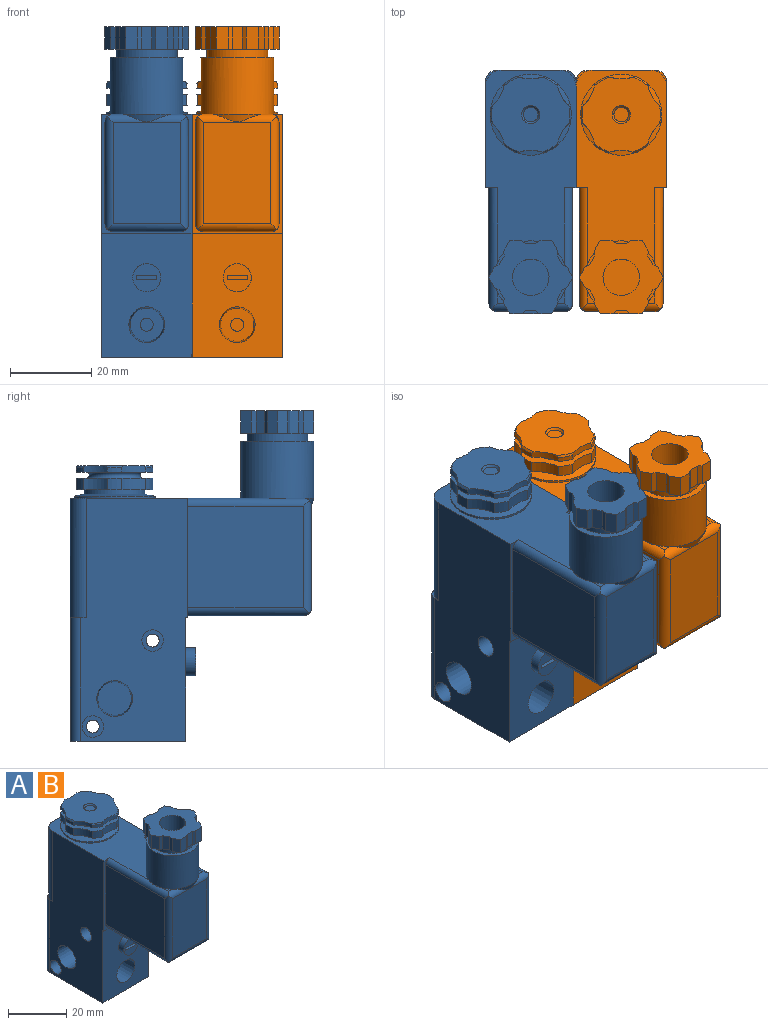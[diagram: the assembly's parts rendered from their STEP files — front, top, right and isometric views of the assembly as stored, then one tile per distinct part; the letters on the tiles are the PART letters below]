
ASSEMBLY  parts=2 mates=1
PART A: 143 faces, bbox 22.3x60.1x81.4 mm
  f0: plane 5.5x2.95mm, normal (0,-1,0), area 16.2mm2, adj f1,f29,f139,f140
  f1: plane 5.5x1mm, normal (0.57,-0.82,0), area 6.7mm2, adj f0,f2,f29,f140
  f2: plane 5.5x2.5mm, normal (0,-1,0), area 13.8mm2, adj f1,f3,f29,f140
  f3: plane 5.5x1mm, normal (-0.57,-0.82,0), area 6.7mm2, adj f2,f4,f29,f140
  f4: plane 5.5x2.95mm, normal (0,-1,0), area 16.2mm2, adj f3,f5,f29,f140
  f5: plane 5.5x2.55mm, normal (0.87,-0.5,0), area 16.2mm2, adj f4,f6,f29,f140
  f6: plane 5.5x1.22mm, normal (1,0.09,0), area 6.7mm2, adj f5,f7,f29,f140
  f7: plane 5.5x2.17mm, normal (0.87,-0.5,0), area 13.8mm2, adj f6,f8,f29,f140
  f8: plane 5.5x1.11mm, normal (0.42,-0.91,0), area 6.7mm2, adj f7,f9,f29,f140
  f9: plane 5.5x2.55mm, normal (0.87,-0.5,0), area 16.2mm2, adj f8,f10,f29,f140
  f10: plane 5.5x2.55mm, normal (0.87,0.5,0), area 16.2mm2, adj f9,f11,f29,f140
  f11: plane 5.5x1.11mm, normal (0.42,0.91,0), area 6.7mm2, adj f10,f12,f29,f140
  f12: plane 5.5x2.17mm, normal (0.87,0.5,0), area 13.8mm2, adj f11,f13,f29,f140
  f13: plane 5.5x1.22mm, normal (1,-0.09,0), area 6.7mm2, adj f12,f14,f29,f140
  f14: plane 5.5x2.55mm, normal (0.87,0.5,0), area 16.2mm2, adj f13,f15,f29,f140
  f15: plane 5.5x2.95mm, normal (0,1,0), area 16.2mm2, adj f14,f16,f29,f140
  f16: plane 5.5x1mm, normal (-0.57,0.82,0), area 6.7mm2, adj f15,f17,f29,f140
  f17: plane 5.5x2.5mm, normal (0,1,0), area 13.8mm2, adj f16,f18,f29,f140
  f18: plane 5.5x1mm, normal (0.57,0.82,0), area 6.7mm2, adj f17,f19,f29,f140
  f19: plane 5.5x2.95mm, normal (0,1,0), area 16.2mm2, adj f18,f20,f29,f140
  f20: plane 5.5x2.55mm, normal (-0.87,0.5,0), area 16.2mm2, adj f19,f21,f29,f140
  f21: plane 5.5x1.22mm, normal (-1,-0.09,0), area 6.7mm2, adj f20,f22,f29,f140
  f22: plane 5.5x2.17mm, normal (-0.87,0.5,0), area 13.8mm2, adj f21,f23,f29,f140
  f23: plane 5.5x1.11mm, normal (-0.42,0.91,0), area 6.7mm2, adj f22,f24,f29,f140
  f24: plane 5.5x2.55mm, normal (-0.87,0.5,0), area 16.2mm2, adj f23,f25,f29,f140
  f25: plane 5.5x2.55mm, normal (-0.87,-0.5,0), area 16.2mm2, adj f24,f26,f29,f140
  f26: plane 5.5x1.11mm, normal (-0.42,-0.91,0), area 6.7mm2, adj f25,f27,f29,f140
  f27: plane 5.5x2.17mm, normal (-0.87,-0.5,0), area 13.8mm2, adj f26,f28,f29,f140
  f28: plane 5.5x1.22mm, normal (-1,0.09,0), area 6.7mm2, adj f27,f29,f139,f140
  f29: plane 20.78x18mm, normal (0,0,-1), area 89.2mm2, adj f0,f1,f2,f3,f4,f5,f6,f7
  f30: cylinder r=7.5mm len=15mm, axis (0,0,-1), area 94.2mm2, adj f29,f31
  f31: plane 18x18mm, normal (0,0,1), area 77.8mm2, adj f30,f32
  f32: cylinder r=9mm len=18mm, axis (0,0,-1), area 791.7mm2, adj f31,f33,f93,f94,f95,f96,f97,f98
  f33: cone r=298.57mm half-angle=17.4deg, axis (0,0,1), area 0mm2, adj f32,f34
  f34: cylinder r=2mm len=29.91mm, axis (0,-1,0), area 88.6mm2, adj f33,f35,f91,f92,f93,f95,f98
  f35: plane 29.5x22.3mm, normal (0,-1,0), area 63.9mm2, adj f34,f36,f40,f41,f42,f43,f86,f87
  f36: plane 28.5x25mm, normal (-1,0,0), area 712.5mm2, adj f35,f37,f40,f90
  f37: cylinder r=2mm len=27.83mm, axis (0,0,1), area 83mm2, adj f36,f38,f39,f40,f90,f95
  f38: plane 25x16.6mm, normal (0,-1,0), area 415mm2, adj f37,f39,f92,f95
  f39: cylinder r=2mm len=19.43mm, axis (1,0,0), area 56.6mm2, adj f37,f38,f40,f41,f42,f92
  f40: cylinder r=2mm len=29.91mm, axis (0,-1,0), area 91.8mm2, adj f35,f36,f37,f39,f41
  f41: plane 28.5x16.6mm, normal (0,0,-1), area 473.1mm2, adj f35,f39,f40,f42
  f42: cylinder r=2mm len=29.91mm, axis (0,-1,0), area 91.8mm2, adj f35,f39,f41,f91,f92
  f43: plane 59.9x26.4mm, normal (1,0,0), area 1419.7mm2, adj f35,f44,f49,f54,f56,f68,f75,f76
  f44: cylinder r=2.65mm len=8mm, axis (-1,0,0), area 133.2mm2, adj f43,f45
  f45: plane 5.3x5.3mm, normal (1,0,0), area 14mm2, adj f44,f46
  f46: cylinder r=1.6mm len=6.3mm, axis (-1,0,0), area 63.3mm2, adj f45,f47
  f47: plane 5.3x5.3mm, normal (-1,0,0), area 14mm2, adj f46,f48
  f48: cylinder r=2.65mm len=8mm, axis (-1,0,0), area 133.2mm2, adj f47,f87
  f49: cylinder r=2.65mm len=8mm, axis (-1,0,0), area 133.2mm2, adj f43,f50
  f50: plane 5.3x5.3mm, normal (1,0,0), area 14mm2, adj f49,f51
  f51: cylinder r=1.6mm len=6.3mm, axis (-1,0,0), area 63.3mm2, adj f50,f52
  f52: plane 5.3x5.3mm, normal (-1,0,0), area 14mm2, adj f51,f53
  f53: cylinder r=2.65mm len=8mm, axis (-1,0,0), area 133.2mm2, adj f52,f87
  f54: cone r=4.15mm half-angle=1.8deg, axis (1,0,0), area 223.2mm2, adj f43,f55
  f55: plane 8.3x8.3mm, normal (1,0,0), area 54.1mm2, adj f54
  f56: plane 30.4x22.3mm, normal (0,-1,0), area 579.5mm2, adj f43,f57,f61,f77,f86,f87
  f57: cone r=4.41mm half-angle=1.8deg, axis (0,-1,0), area 267.3mm2, adj f56,f58
  f58: plane 8.19x8.19mm, normal (0,-1,0), area 44.7mm2, adj f57,f59
  f59: cylinder r=1.6mm len=3.2mm, axis (0,-1,0), area 30.2mm2, adj f58,f60
  f60: plane 3.2x3.2mm, normal (0,-1,0), area 8mm2, adj f59
  f61: cylinder r=3.45mm len=6.9mm, axis (0,-1,0), area 54.2mm2, adj f56,f62
  f62: plane 6.9x6.9mm, normal (0,-1,0), area 32.4mm2, adj f61,f63,f65,f66,f67
  f63: plane 5x1mm, normal (0,0,1), area 5mm2, adj f62,f64,f65,f67
  f64: plane 5x1mm, normal (0,-1,0), area 5mm2, adj f63,f65,f66,f67
  f65: plane 1x1mm, normal (-1,0,0), area 1mm2, adj f62,f63,f64,f66
  f66: plane 5x1mm, normal (0,0,-1), area 5mm2, adj f62,f64,f65,f67
  f67: plane 1x1mm, normal (1,0,0), area 1mm2, adj f62,f63,f64,f66
  f68: cylinder r=4mm len=29.5mm, axis (0,0,1), area 185.4mm2, adj f43,f69,f74,f75,f98
  f69: plane 29.5x14.3mm, normal (0,1,0), area 421.9mm2, adj f68,f70,f74,f98
  f70: cylinder r=4mm len=29.5mm, axis (0,0,1), area 185.4mm2, adj f69,f71,f74,f87,f98
  f71: plane 3.9x3.11mm, normal (0,0,1), area 1.8mm2, adj f70,f72,f73,f87
  f72: cylinder r=2.5mm len=30.4mm, axis (0,0,1), area 119.4mm2, adj f71,f73,f77,f87
  f73: plane 30.4x17.3mm, normal (0,1,0), area 525.9mm2, adj f71,f72,f74,f75,f76,f77
  f74: plane 16.08x0.1mm, normal (0,0,-1), area 1.5mm2, adj f68,f69,f70,f73
  f75: plane 3.9x3.11mm, normal (0,0,1), area 1.8mm2, adj f43,f68,f73,f76
  f76: cylinder r=2.5mm len=30.4mm, axis (0,0,1), area 119.4mm2, adj f43,f73,f75,f77
  f77: plane 28.4x22.3mm, normal (0,0,-1), area 605.5mm2, adj f43,f56,f72,f73,f76,f78,f82,f87
  f78: cone r=2mm half-angle=45deg, axis (0,0,-1), area 6.1mm2, adj f77,f79
  f79: cylinder r=1.62mm len=7.24mm, axis (0,0,-1), area 73.8mm2, adj f78,f80
  f80: cone r=1.62mm half-angle=45deg, axis (0,0,1), area 6.1mm2, adj f79,f81
  f81: plane 4x4mm, normal (0,0,-1), area 12.6mm2, adj f80
  f82: cone r=2mm half-angle=45deg, axis (0,0,-1), area 6.1mm2, adj f77,f83
  f83: cylinder r=1.62mm len=7.24mm, axis (0,0,-1), area 73.8mm2, adj f82,f84
  f84: cone r=1.62mm half-angle=45deg, axis (0,0,1), area 6.1mm2, adj f83,f85
  f85: plane 4x4mm, normal (0,0,-1), area 12.6mm2, adj f84
  f86: plane 22.3x0.5mm, normal (0,0,-1), area 11.1mm2, adj f35,f43,f56,f87
  f87: plane 59.9x26.4mm, normal (-1,0,0), area 1419.7mm2, adj f35,f48,f53,f56,f70,f71,f72,f77
  f88: cone r=4.41mm half-angle=1.8deg, axis (-1,0,0), area 223.2mm2, adj f87,f89
  f89: plane 8.3x8.3mm, normal (-1,0,0), area 54.1mm2, adj f88
  f90: cylinder r=2mm len=29.91mm, axis (0,-1,0), area 88.6mm2, adj f35,f36,f37,f95,f96,f97,f98
  f91: plane 28.5x25mm, normal (1,0,0), area 712.5mm2, adj f34,f35,f42,f92
  f92: cylinder r=2mm len=27.83mm, axis (0,0,1), area 83mm2, adj f34,f38,f39,f42,f91,f95
  f93: plane 2.92x1.97mm, normal (0,0,1), area 2.5mm2, adj f32,f34,f95
  f94: cone r=298.57mm half-angle=17.4deg, axis (0,0,1), area 0mm2, adj f32,f95
  f95: cylinder r=2mm len=19.43mm, axis (1,0,0), area 32.5mm2, adj f32,f34,f37,f38,f90,f92,f93,f94
  f96: plane 2.92x1.97mm, normal (0,0,1), area 2.5mm2, adj f32,f90,f95
  f97: cone r=298.57mm half-angle=17.4deg, axis (0,0,1), area 0mm2, adj f32,f90
  f98: plane 47.62x22.3mm, normal (0,0,1), area 568.6mm2, adj f32,f34,f35,f43,f68,f69,f70,f87
  f99: cylinder r=10mm len=20mm, axis (0,0,1), area 31.4mm2, adj f98,f100
  f100: cone r=7.5mm half-angle=78.7deg, axis (0,0,-1), area 140.2mm2, adj f99,f101
  f101: cylinder r=7.5mm len=15mm, axis (0,0,1), area 47.1mm2, adj f100,f102
  f102: plane 20x18.83mm, normal (0,0,-1), area 104.9mm2, adj f101,f103,f128,f129,f130,f131,f132,f133
  f103: cylinder r=9.5mm len=6.73mm, axis (0,0,-1), area 19.6mm2, adj f102,f104,f128,f138
  f104: plane 20x18.83mm, normal (0,0,1), area 127.7mm2, adj f103,f105,f128,f129,f130,f131,f132,f133
  f105: torus R=7mm, axis (0,0,-1), area 96.6mm2, adj f104,f106
  f106: plane 20x18.83mm, normal (0,0,-1), area 127.7mm2, adj f105,f107,f117,f118,f119,f120,f121,f122
  f107: cylinder r=9.5mm len=6.73mm, axis (0,0,-1), area 11.1mm2, adj f106,f108,f109,f116,f117,f127
  f108: cone r=9.66mm half-angle=33.9deg, axis (0,0,-1), area 2.4mm2, adj f107,f109,f117,f118
  f109: plane 19.33x18.47mm, normal (0,0,1), area 258.1mm2, adj f107,f108,f110,f112,f113,f114,f115,f116
  f110: cone r=1.8mm half-angle=40.4deg, axis (0,0,1), area 8.3mm2, adj f109,f111
  f111: plane 3.6x3.6mm, normal (0,0,1), area 10.2mm2, adj f110
  f112: cone r=9.66mm half-angle=33.9deg, axis (0,0,-1), area 2.4mm2, adj f109,f124,f125,f126
  f113: cone r=9.66mm half-angle=33.9deg, axis (0,0,-1), area 2.4mm2, adj f109,f122,f123,f124
  f114: cone r=9.66mm half-angle=33.9deg, axis (0,0,-1), area 2.4mm2, adj f109,f120,f121,f122
  f115: cone r=9.66mm half-angle=33.9deg, axis (0,0,-1), area 2.4mm2, adj f109,f118,f119,f120
  f116: cone r=9.66mm half-angle=33.9deg, axis (0,0,-1), area 2.4mm2, adj f107,f109,f126,f127
  f117: cylinder r=10mm len=3.11mm, axis (0,0,1), area 4.1mm2, adj f106,f107,f108,f118
  f118: cylinder r=9.5mm len=5.83mm, axis (0,0,-1), area 11.1mm2, adj f106,f108,f109,f115,f117,f119
  f119: cylinder r=10mm len=3.59mm, axis (0,0,1), area 4.1mm2, adj f106,f115,f118,f120
  f120: cylinder r=9.5mm len=5.83mm, axis (0,0,-1), area 11.1mm2, adj f106,f109,f114,f115,f119,f121
  f121: cylinder r=10mm len=3.11mm, axis (0,0,1), area 4.1mm2, adj f106,f114,f120,f122
  f122: cylinder r=9.5mm len=6.73mm, axis (0,0,-1), area 11.1mm2, adj f106,f109,f113,f114,f121,f123
  f123: cylinder r=10mm len=3.11mm, axis (0,0,1), area 4.1mm2, adj f106,f113,f122,f124
  f124: cylinder r=9.5mm len=5.83mm, axis (0,0,-1), area 11.1mm2, adj f106,f109,f112,f113,f123,f125
  f125: cylinder r=10mm len=3.59mm, axis (0,0,1), area 4.1mm2, adj f106,f112,f124,f126
  f126: cylinder r=9.5mm len=5.83mm, axis (0,0,-1), area 11.1mm2, adj f106,f109,f112,f116,f125,f127
  f127: cylinder r=10mm len=3.11mm, axis (0,0,1), area 4.1mm2, adj f106,f107,f116,f126
  f128: cylinder r=10mm len=3.11mm, axis (0,0,1), area 10.3mm2, adj f102,f103,f104,f129
  f129: cylinder r=9.5mm len=5.83mm, axis (0,0,-1), area 19.6mm2, adj f102,f104,f128,f130
  f130: cylinder r=10mm len=3.59mm, axis (0,0,1), area 10.3mm2, adj f102,f104,f129,f131
  f131: cylinder r=9.5mm len=5.83mm, axis (0,0,-1), area 19.6mm2, adj f102,f104,f130,f132
  f132: cylinder r=10mm len=3.11mm, axis (0,0,1), area 10.3mm2, adj f102,f104,f131,f133
  f133: cylinder r=9.5mm len=6.73mm, axis (0,0,-1), area 19.6mm2, adj f102,f104,f132,f134
  f134: cylinder r=10mm len=3.11mm, axis (0,0,1), area 10.3mm2, adj f102,f104,f133,f135
  f135: cylinder r=9.5mm len=5.83mm, axis (0,0,-1), area 19.6mm2, adj f102,f104,f134,f136
  f136: cylinder r=10mm len=3.59mm, axis (0,0,1), area 10.3mm2, adj f102,f104,f135,f137
  f137: cylinder r=9.5mm len=5.83mm, axis (0,0,-1), area 19.6mm2, adj f102,f104,f136,f138
  f138: cylinder r=10mm len=3.11mm, axis (0,0,1), area 10.3mm2, adj f102,f103,f104,f137
  f139: plane 5.5x2.55mm, normal (-0.87,-0.5,0), area 16.2mm2, adj f0,f28,f29,f140
  f140: plane 20.78x18mm, normal (0,0,1), area 202.3mm2, adj f0,f1,f2,f3,f4,f5,f6,f7
  f141: cylinder r=4.5mm len=21.5mm, axis (0,0,-1), area 607.9mm2, adj f140,f142
  f142: plane 9x9mm, normal (0,0,1), area 63.6mm2, adj f141
PART B: same geometry as A
PLACE A t=(-65.31,0.53,14.33)mm
PLACE B t=(-43.01,0.53,14.33)mm
MATE fastened B.f87 <-> A.f43  axis (-1,0,0) through (-54.16,12.71,45.32)mm
